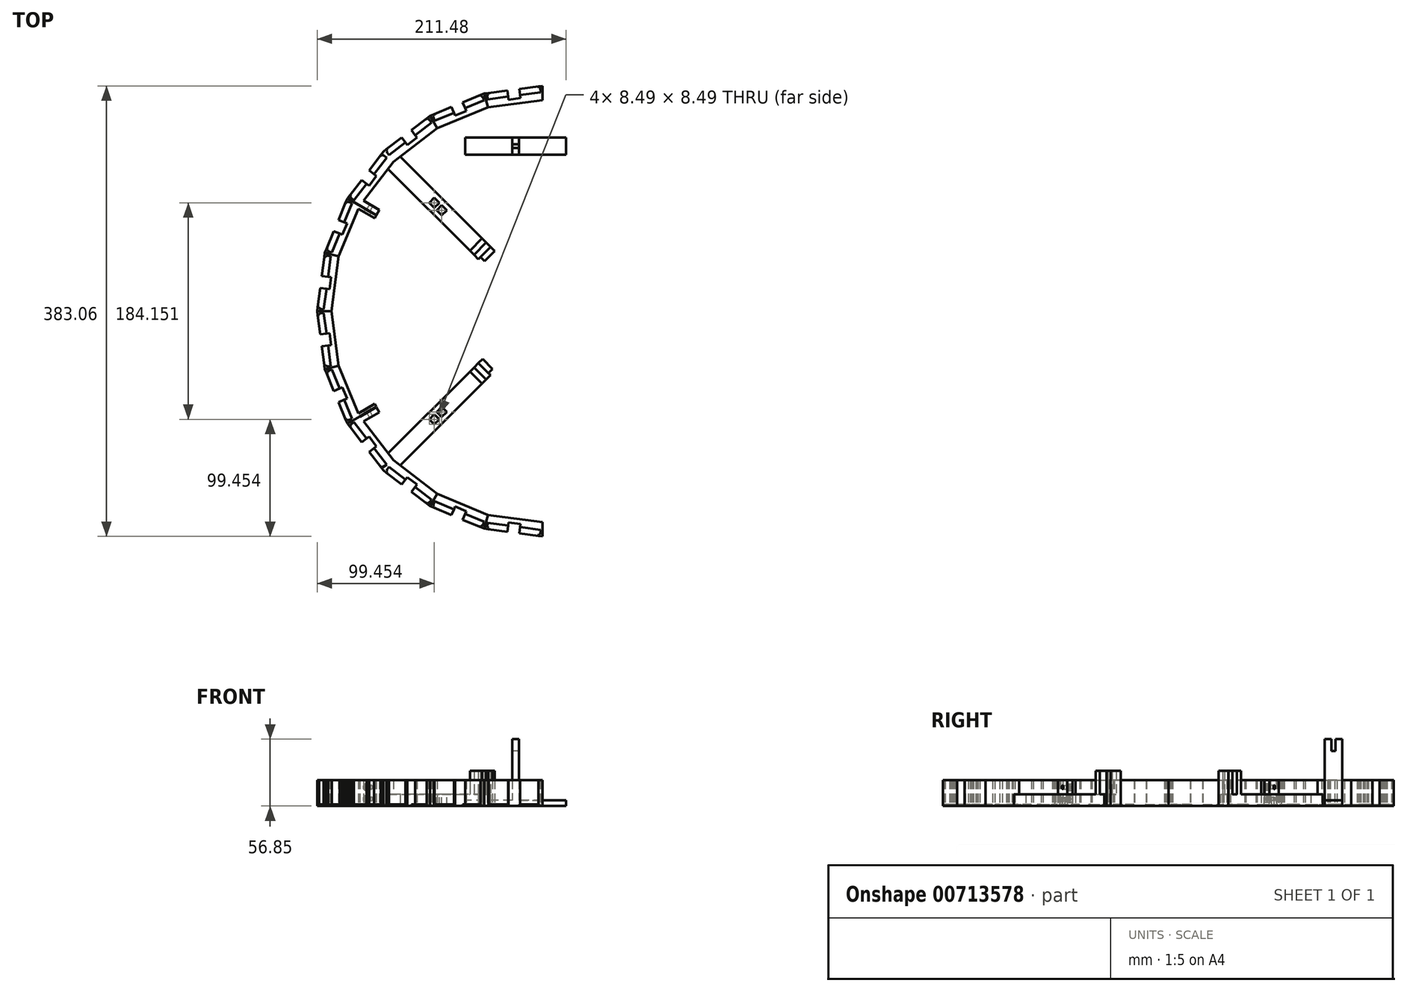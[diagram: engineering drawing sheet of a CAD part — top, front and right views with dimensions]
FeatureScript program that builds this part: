
annotation { "Feature Type Name" : "Feature", "Feature Type Description" : "" }
export const myFeature = defineFeature(function(context is Context, id is Id, definition is map)
    precondition{}
    {
        {
            var Q0;
            Q0=qCreatedBy(makeId("Top.planeOp"),FACE);
            var sketch = newSketch(context, id + "F0", { "sketchPlane" : qUnion([Q0])});
            skCircle(sketch, "E0.cCircle", {"center": v(0, 0) * mm, "radius": 75 * mm, "construction": true});
            skLineSegment(sketch, "E0.0", {"start": v(75, 31.07) * mm, "end": v(75, -31.07) * mm, "construction": true});
            skLineSegment(sketch, "E0.1", {"start": v(75, -31.07) * mm, "end": v(31.07, -75) * mm, "construction": true});
            skLineSegment(sketch, "E0.2", {"start": v(31.07, -75) * mm, "end": v(-31.07, -75) * mm, "construction": true});
            skLineSegment(sketch, "E0.3", {"start": v(-31.07, -75) * mm, "end": v(-75, -31.07) * mm, "construction": true});
            skLineSegment(sketch, "E0.4", {"start": v(-75, -31.07) * mm, "end": v(-75, 31.07) * mm, "construction": true});
            skLineSegment(sketch, "E0.5", {"start": v(-75, 31.07) * mm, "end": v(-31.07, 75) * mm, "construction": true});
            skLineSegment(sketch, "E0.6", {"start": v(-31.07, 75) * mm, "end": v(31.07, 75) * mm, "construction": true});
            skLineSegment(sketch, "E0.7", {"start": v(31.07, 75) * mm, "end": v(75, 31.07) * mm, "construction": true});
            skPoint(sketch, "E0.0.midPoint", {"position": v(74.36, -9.79) * mm});
            skPoint(sketch, "E1.endSnap0", {"position": v(0, -75) * mm});
            skArc(sketch, "E2.cCircle", {"start": v(0.47, 189.9) * mm, "mid": v(-189.9, 0.2) * mm, "end": v(0.07, -189.9) * mm, "construction": true});
            skLineSegment(sketch, "E2.1", {"start": v(0, -191.53) * mm, "end": v(-49.57, -185) * mm});
            skLineSegment(sketch, "E2.2", {"start": v(-49.57, -185) * mm, "end": v(-52.85, -183.65) * mm});
            skLineSegment(sketch, "E2.3", {"start": v(-95.77, -165.87) * mm, "end": v(-135.43, -135.43) * mm});
            skLineSegment(sketch, "E2.4", {"start": v(-135.43, -135.43) * mm, "end": v(-165.87, -95.77) * mm});
            skLineSegment(sketch, "E2.5", {"start": v(-165.87, -95.77) * mm, "end": v(-185, -49.57) * mm});
            skLineSegment(sketch, "E2.6", {"start": v(-185, -49.57) * mm, "end": v(-191.53, 0) * mm});
            skLineSegment(sketch, "E2.7", {"start": v(-191.53, 0) * mm, "end": v(-185, 49.57) * mm});
            skLineSegment(sketch, "E2.8", {"start": v(-185, 49.57) * mm, "end": v(-165.91, 95.67) * mm});
            skLineSegment(sketch, "E2.9", {"start": v(-165.81, 95.85) * mm, "end": v(-135.43, 135.43) * mm});
            skLineSegment(sketch, "E2.10", {"start": v(-135.43, 135.43) * mm, "end": v(-95.77, 165.87) * mm});
            skLineSegment(sketch, "E2.11", {"start": v(-95.77, 165.87) * mm, "end": v(-49.57, 185) * mm});
            skLineSegment(sketch, "E2.12", {"start": v(-49.57, 185) * mm, "end": v(0.47, 191.6) * mm});
            skLineSegment(sketch, "E3", {"start": v(0, 0) * mm, "end": v(-188.27, 24.79) * mm, "construction": true});
            skLineSegment(sketch, "E4.0", {"start": v(-46.44, 173.32) * mm, "end": v(0.46, 179.49) * mm});
            skLineSegment(sketch, "E4.1", {"start": v(-89.71, 155.39) * mm, "end": v(-46.44, 173.32) * mm});
            skLineSegment(sketch, "E4.2", {"start": v(-126.88, -126.88) * mm, "end": v(-155.39, -89.71) * mm});
            skLineSegment(sketch, "E4.3", {"start": v(-89.71, -155.39) * mm, "end": v(-126.88, -126.88) * mm});
            skLineSegment(sketch, "E4.4", {"start": v(-46.44, -173.32) * mm, "end": v(-89.71, -155.39) * mm});
            skLineSegment(sketch, "E4.5", {"start": v(0.5, -179.5) * mm, "end": v(-46.44, -173.32) * mm});
            skLineSegment(sketch, "E4.6", {"start": v(-155.39, -89.71) * mm, "end": v(-173.32, -46.44) * mm});
            skLineSegment(sketch, "E4.7", {"start": v(-173.32, -46.44) * mm, "end": v(-179.43, 0) * mm});
            skLineSegment(sketch, "E4.9", {"start": v(-173.32, 46.44) * mm, "end": v(-155.43, 89.62) * mm});
            skLineSegment(sketch, "E4.10", {"start": v(-155.33, 89.8) * mm, "end": v(-126.88, 126.88) * mm});
            skLineSegment(sketch, "E4.11", {"start": v(-126.88, 126.88) * mm, "end": v(-89.71, 155.39) * mm});
            skLineSegment(sketch, "E5", {"start": v(-72.67, -175.44) * mm, "end": v(-70.64, -170.54) * mm, "construction": true});
            skLineSegment(sketch, "E6", {"start": v(-65.88, -172.51) * mm, "end": v(-49.62, -179.25) * mm});
            skLineSegment(sketch, "E7", {"start": v(-75.4, -168.57) * mm, "end": v(-91.66, -161.84) * mm});
            skLineSegment(sketch, "E8", {"start": v(-49.62, -179.25) * mm, "end": v(-51.15, -182.94) * mm});
            skLineSegment(sketch, "E9", {"start": v(-91.66, -161.84) * mm, "end": v(-93.2, -165.53) * mm});
            skLineSegment(sketch, "E10", {"start": v(-93.2, -165.53) * mm, "end": v(-91.99, -166.03) * mm});
            skLineSegment(sketch, "E11", {"start": v(-91.99, -166.03) * mm, "end": v(-92.49, -167.23) * mm});
            skLineSegment(sketch, "E12", {"start": v(-51.15, -182.94) * mm, "end": v(-52.35, -182.45) * mm});
            skLineSegment(sketch, "E13", {"start": v(-52.35, -182.45) * mm, "end": v(-52.85, -183.65) * mm});
            skLineSegment(sketch, "E14.trimOffspring", {"start": v(-92.49, -167.23) * mm, "end": v(-95.77, -165.87) * mm});
            skLineSegment(sketch, "E15", {"start": v(-72.67, -175.44) * mm, "end": v(-69.65, -168.14) * mm, "construction": true});
            skLineSegment(sketch, "E16", {"start": v(-69.65, -168.14) * mm, "end": v(-64.89, -170.11) * mm});
            skLineSegment(sketch, "E17", {"start": v(-69.65, -168.14) * mm, "end": v(-74.4, -166.17) * mm});
            skLineSegment(sketch, "E18", {"start": v(-74.4, -166.17) * mm, "end": v(-75.4, -168.57) * mm});
            skLineSegment(sketch, "E19", {"start": v(-64.89, -170.11) * mm, "end": v(-65.88, -172.51) * mm});
            skLineSegment(sketch, "E20", {"start": v(-49.57, -185) * mm, "end": v(-46.44, -173.32) * mm});
            skLineSegment(sketch, "E21", {"start": v(-95.77, -165.87) * mm, "end": v(-89.71, -155.39) * mm});
            skLineSegment(sketch, "E22", {"start": v(-52.85, -183.65) * mm, "end": v(-92.49, -167.23) * mm});
            skLineSegment(sketch, "E23", {"start": v(-75.4, -168.57) * mm, "end": v(-77.43, -173.47) * mm});
            skLineSegment(sketch, "E24", {"start": v(-65.88, -172.51) * mm, "end": v(-67.91, -177.4) * mm, "construction": true});
            skLineSegment(sketch, "E25", {"start": v(-67.91, -177.4) * mm, "end": v(-65.88, -172.51) * mm});
            skLineSegment(sketch, "E26", {"start": v(-77.43, -173.47) * mm, "end": v(-75.4, -168.57) * mm, "construction": true});
            skLineSegment(sketch, "E27", {"start": v(-53.03, 53.03) * mm, "end": v(-126.88, 126.88) * mm, "construction": true});
            skLineSegment(sketch, "E28.0", {"start": v(-47.87, 58.2) * mm, "end": v(-121.03, 131.36) * mm});
            skLineSegment(sketch, "E29.0", {"start": v(-58.2, 47.87) * mm, "end": v(-131.36, 121.03) * mm});
            skLineSegment(sketch, "E30", {"start": v(-61.73, 51.4) * mm, "end": v(-51.4, 61.73) * mm});
            skLineSegment(sketch, "E31", {"start": v(-47.87, 58.2) * mm, "end": v(-44.2, 54.52) * mm});
            skLineSegment(sketch, "E32", {"start": v(-58.2, 47.87) * mm, "end": v(-54.52, 44.2) * mm});
            skLineSegment(sketch, "E33", {"start": v(-54.52, 44.2) * mm, "end": v(-44.2, 54.52) * mm});
            skLineSegment(sketch, "E34", {"start": v(-44.2, 54.52) * mm, "end": v(-40.66, 50.98) * mm});
            skLineSegment(sketch, "E35", {"start": v(-40.66, 50.98) * mm, "end": v(-49.14, 42.5) * mm});
            skLineSegment(sketch, "E36", {"start": v(-49.14, 42.5) * mm, "end": v(-52.68, 46.03) * mm});
            skLineSegment(sketch, "E37", {"start": v(-47.87, 58.2) * mm, "end": v(-58.2, 47.87) * mm});
            skLineSegment(sketch, "E38.1.0", {"start": v(-50.98, -40.66) * mm, "end": v(-42.5, -49.14) * mm});
            skLineSegment(sketch, "E38.1.1", {"start": v(-54.52, -44.2) * mm, "end": v(-50.98, -40.66) * mm});
            skLineSegment(sketch, "E38.1.2", {"start": v(-58.2, -47.87) * mm, "end": v(-54.52, -44.2) * mm});
            skLineSegment(sketch, "E38.1.3", {"start": v(-58.2, -47.87) * mm, "end": v(-47.87, -58.2) * mm});
            skLineSegment(sketch, "E38.1.4", {"start": v(-51.4, -61.73) * mm, "end": v(-61.73, -51.4) * mm});
            skLineSegment(sketch, "E38.1.5", {"start": v(-44.2, -54.52) * mm, "end": v(-54.52, -44.2) * mm});
            skLineSegment(sketch, "E38.1.6", {"start": v(-47.87, -58.2) * mm, "end": v(-44.2, -54.52) * mm});
            skLineSegment(sketch, "E38.1.7", {"start": v(-47.87, -58.2) * mm, "end": v(-121.03, -131.36) * mm});
            skLineSegment(sketch, "E38.1.8", {"start": v(-58.2, -47.87) * mm, "end": v(-131.36, -121.03) * mm});
            skLineSegment(sketch, "E38.anchor1", {"start": v(0, 0) * mm, "end": v(-49.14, 42.5) * mm, "construction": true});
            skLineSegment(sketch, "E38.anchor2", {"start": v(0, 0) * mm, "end": v(-42.5, -49.14) * mm, "construction": true});
            skLineSegment(sketch, "E39", {"start": v(-179.43, 0) * mm, "end": v(-191.53, 0) * mm});
            skLineSegment(sketch, "E40", {"start": v(0.07, -189.9) * mm, "end": v(0.47, 191.6) * mm, "construction": true});
            skPoint(sketch, "E41.orphan", {"position": v(0.5, 222.53) * mm});
            skLineSegment(sketch, "E42", {"start": v(-42.5, -49.14) * mm, "end": v(-46.03, -52.68) * mm});
            skLineSegment(sketch, "E43", {"start": v(-179.43, 0) * mm, "end": v(-173.32, 46.44) * mm});
            skLineSegment(sketch, "E44", {"start": v(-141.21, 81.64) * mm, "end": v(-138.71, 85.98) * mm});
            skLineSegment(sketch, "E45", {"start": v(-138.71, 85.98) * mm, "end": v(-152.26, 93.8) * mm});
            skLineSegment(sketch, "E46", {"start": v(-141.31, 81.47) * mm, "end": v(-142.76, 78.96) * mm});
            skLineSegment(sketch, "E47", {"start": v(-142.76, 78.96) * mm, "end": v(-156.55, 86.92) * mm});
            skLineSegment(sketch, "E48", {"start": v(0, 0) * mm, "end": v(-165.87, 95.77) * mm, "construction": true});
            skLineSegment(sketch, "E49", {"start": v(-141.21, 81.64) * mm, "end": v(-165.81, 95.85) * mm});
            skLineSegment(sketch, "E50", {"start": v(-165.91, 95.67) * mm, "end": v(-141.31, 81.47) * mm});
            skLineSegment(sketch, "E51", {"start": v(-155.43, 89.62) * mm, "end": v(-155.33, 89.8) * mm});
            skLineSegment(sketch, "E52", {"start": v(-165.91, 95.67) * mm, "end": v(-165.87, 95.77) * mm});
            skLineSegment(sketch, "E53", {"start": v(-165.87, 95.77) * mm, "end": v(-165.81, 95.85) * mm});
            skLineSegment(sketch, "E54.1.0", {"start": v(-141.31, -81.47) * mm, "end": v(-142.76, -78.96) * mm});
            skLineSegment(sketch, "E54.1.2", {"start": v(-141.31, -81.47) * mm, "end": v(-165.91, -95.67) * mm});
            skLineSegment(sketch, "E54.1.3", {"start": v(-165.81, -95.85) * mm, "end": v(-141.21, -81.64) * mm});
            skLineSegment(sketch, "E54.1.4", {"start": v(-155.33, -89.8) * mm, "end": v(-155.43, -89.62) * mm});
            skLineSegment(sketch, "E54.1.5", {"start": v(-138.71, -85.98) * mm, "end": v(-152.26, -93.8) * mm});
            skLineSegment(sketch, "E54.1.6", {"start": v(-141.21, -81.64) * mm, "end": v(-138.71, -85.98) * mm});
            skLineSegment(sketch, "E54.1.7", {"start": v(-165.81, -95.85) * mm, "end": v(-165.87, -95.77) * mm});
            skLineSegment(sketch, "E54.1.8", {"start": v(-165.87, -95.77) * mm, "end": v(-165.91, -95.67) * mm});
            skLineSegment(sketch, "E54.1.9", {"start": v(0, 0) * mm, "end": v(-165.87, -95.77) * mm, "construction": true});
            skLineSegment(sketch, "E54.anchor1", {"start": v(0, 0) * mm, "end": v(-165.91, 95.67) * mm, "construction": true});
            skLineSegment(sketch, "E54.anchor2", {"start": v(0, 0) * mm, "end": v(-165.81, -95.85) * mm, "construction": true});
            skLineSegment(sketch, "E55", {"start": v(-142.76, -78.96) * mm, "end": v(-156.55, -86.92) * mm});
            skSolve(sketch);
        }
        {
            var Q0;
            Q0=makeQuery(id+"F0.imprint","IMPRINT",FACE,{"disambiguationData":[TD([[makeQuery(id+"F0.imprint","IMPRINT",EDGE,{"derivedFrom":sQuery(id+"F0.wireOp",EDGE,"E2.2")}),-1.0]])]});
            extrude(context, id + "F1", {"entities" : qUnion([Q0]), "depth" : 22 * mm, "offsetDistance" : 25 * mm});
        }
        {
            var Q0;
            Q0=makeQuery(id+"F0.imprint","IMPRINT",FACE,{"disambiguationData":[TD([[makeQuery(id+"F0.imprint","IMPRINT",EDGE,{"derivedFrom":sQuery(id+"F0.wireOp",EDGE,"E6")}),-1.0]])]});
            var Q1;
            Q1=makeQuery(id+"F0.imprint","IMPRINT",FACE,{"disambiguationData":[TD([[makeQuery(id+"F0.imprint","IMPRINT",EDGE,{"derivedFrom":sQuery(id+"F0.wireOp",EDGE,"E7")}),1.0]])]});
            extrude(context, id + "F2", {"entities" : qUnion([Q0, Q1]), "operationType" : NewBodyOperationType.ADD, "depth" : 1.5 * mm, "offsetDistance" : 25 * mm});
        }
        {
            var Q0;
            Q0=qCreatedBy(makeId("Front.planeOp"),FACE);
            var sketch = newSketch(context, id + "F3", { "sketchPlane" : qUnion([Q0])});
            skLineSegment(sketch, "E56", {"start": v(0, 0) * mm, "end": v(0, 23.59) * mm, "construction": true});
            skSolve(sketch);
        }
        {
            var Q0;
            Q0=makeQuery(id+"F1.opExtrude","SWEPT_BODY",BODY,{"disambiguationData":[OSD([sQuery(id+"F0.wireOp",EDGE,"E2.2"),sQuery(id+"F0.wireOp",EDGE,"E4.4"),sQuery(id+"F0.wireOp",EDGE,"E6"),sQuery(id+"F0.wireOp",EDGE,"E7"),sQuery(id+"F0.wireOp",EDGE,"E8"),sQuery(id+"F0.wireOp",EDGE,"E9"),sQuery(id+"F0.wireOp",EDGE,"E10"),sQuery(id+"F0.wireOp",EDGE,"E11"),sQuery(id+"F0.wireOp",EDGE,"E12"),sQuery(id+"F0.wireOp",EDGE,"E13"),sQuery(id+"F0.wireOp",EDGE,"E14.trimOffspring"),sQuery(id+"F0.wireOp",EDGE,"E16"),sQuery(id+"F0.wireOp",EDGE,"E17"),sQuery(id+"F0.wireOp",EDGE,"E18"),sQuery(id+"F0.wireOp",EDGE,"E19"),sQuery(id+"F0.wireOp",EDGE,"E20"),sQuery(id+"F0.wireOp",EDGE,"E21")])]});
            var Q1;
            Q1=sQuery(id+"F3.wireOp",EDGE,"E56");
            transform(context, id + "F4", {"entities" : qUnion([Q0]), "transformType" : TransformType.ROTATION, "transformAxis" : qUnion([Q1]), "angle" : 15 * degree, "makeCopy" : true});
        }
        {
            var Q0;
            Q0=makeQuery(id+"F1.opExtrude","SWEPT_BODY",BODY,{"disambiguationData":[OSD([sQuery(id+"F0.wireOp",EDGE,"E2.2"),sQuery(id+"F0.wireOp",EDGE,"E4.4"),sQuery(id+"F0.wireOp",EDGE,"E6"),sQuery(id+"F0.wireOp",EDGE,"E7"),sQuery(id+"F0.wireOp",EDGE,"E8"),sQuery(id+"F0.wireOp",EDGE,"E9"),sQuery(id+"F0.wireOp",EDGE,"E10"),sQuery(id+"F0.wireOp",EDGE,"E11"),sQuery(id+"F0.wireOp",EDGE,"E12"),sQuery(id+"F0.wireOp",EDGE,"E13"),sQuery(id+"F0.wireOp",EDGE,"E14.trimOffspring"),sQuery(id+"F0.wireOp",EDGE,"E16"),sQuery(id+"F0.wireOp",EDGE,"E17"),sQuery(id+"F0.wireOp",EDGE,"E18"),sQuery(id+"F0.wireOp",EDGE,"E19"),sQuery(id+"F0.wireOp",EDGE,"E20"),sQuery(id+"F0.wireOp",EDGE,"E21")])]});
            var Q1;
            Q1=sQuery(id+"F3.wireOp",EDGE,"E56");
            circularPattern(context, id + "F5", {"entities" : qUnion([Q0]), "axis" : qUnion([Q1]), "angle" : 150 * degree, "instanceCount" : 11, "oppositeDirection" : true, "equalSpace" : true});
        }
        {
            var Q0;
            {var subQ3=sQuery(id+"F0.wireOp",EDGE,"E30");Q0=makeQuery(id+"F0.imprint","IMPRINT",FACE,{"disambiguationData":[TD([[makeQuery(id+"F0.imprint","IMPRINT",EDGE,{"derivedFrom":subQ3}),1.0]])]});}
            var Q1;
            {var subQ2=sQuery(id+"F0.wireOp",EDGE,"E30");Q1=makeQuery(id+"F0.imprint","IMPRINT",FACE,{"disambiguationData":[TD([[makeQuery(id+"F0.imprint","IMPRINT",EDGE,{"derivedFrom":subQ2}),-1.0]])]});}
            var Q2;
            {var subQ1=sQuery(id+"F0.wireOp",EDGE,"E31");Q2=makeQuery(id+"F0.imprint","IMPRINT",FACE,{"disambiguationData":[TD([[makeQuery(id+"F0.imprint","IMPRINT",EDGE,{"derivedFrom":subQ1}),-1.0]])]});}
            var Q3;
            {var subQ0=sQuery(id+"F0.wireOp",EDGE,"E34");Q3=makeQuery(id+"F0.imprint","IMPRINT",FACE,{"disambiguationData":[TD([[makeQuery(id+"F0.imprint","IMPRINT",EDGE,{"derivedFrom":subQ0}),-1.0]])]});}
            var Q4;
            {var subQ1=sQuery(id+"F0.wireOp",EDGE,"E38.1.4");Q4=makeQuery(id+"F0.imprint","IMPRINT",FACE,{"disambiguationData":[TD([[makeQuery(id+"F0.imprint","IMPRINT",EDGE,{"derivedFrom":subQ1}),1.0]])]});}
            var Q5;
            {var subQ0=sQuery(id+"F0.wireOp",EDGE,"E38.1.3");Q5=makeQuery(id+"F0.imprint","IMPRINT",FACE,{"disambiguationData":[TD([[makeQuery(id+"F0.imprint","IMPRINT",EDGE,{"derivedFrom":subQ0}),-1.0]])]});}
            var Q6;
            {var subQ1=sQuery(id+"F0.wireOp",EDGE,"E38.1.2");Q6=makeQuery(id+"F0.imprint","IMPRINT",FACE,{"disambiguationData":[TD([[makeQuery(id+"F0.imprint","IMPRINT",EDGE,{"derivedFrom":subQ1}),-1.0]])]});}
            var Q7;
            Q7=makeQuery(id+"F0.imprint","IMPRINT",FACE,{"disambiguationData":[TD([[makeQuery(id+"F0.imprint","IMPRINT",EDGE,{"derivedFrom":sQuery(id+"F0.wireOp",EDGE,"E38.1.0")}),-1.0]])]});
            extrude(context, id + "F6", {"entities" : qUnion([Q0, Q1, Q2, Q3, Q4, Q5, Q6, Q7]), "operationType" : NewBodyOperationType.ADD, "depth" : 5 * mm, "offsetDistance" : 25 * mm});
        }
        {
            var Q0;
            {var subQ2=sQuery(id+"F0.wireOp",EDGE,"E30");Q0=makeQuery(id+"F0.imprint","IMPRINT",FACE,{"disambiguationData":[TD([[makeQuery(id+"F0.imprint","IMPRINT",EDGE,{"derivedFrom":subQ2}),-1.0]])]});}
            var Q1;
            {var subQ0=sQuery(id+"F0.wireOp",EDGE,"E34");Q1=makeQuery(id+"F0.imprint","IMPRINT",FACE,{"disambiguationData":[TD([[makeQuery(id+"F0.imprint","IMPRINT",EDGE,{"derivedFrom":subQ0}),-1.0]])]});}
            var Q2;
            Q2=makeQuery(id+"F0.imprint","IMPRINT",FACE,{"disambiguationData":[TD([[makeQuery(id+"F0.imprint","IMPRINT",EDGE,{"derivedFrom":sQuery(id+"F0.wireOp",EDGE,"E38.1.0")}),-1.0]])]});
            var Q3;
            {var subQ0=sQuery(id+"F0.wireOp",EDGE,"E38.1.3");Q3=makeQuery(id+"F0.imprint","IMPRINT",FACE,{"disambiguationData":[TD([[makeQuery(id+"F0.imprint","IMPRINT",EDGE,{"derivedFrom":subQ0}),-1.0]])]});}
            extrude(context, id + "F7", {"entities" : qUnion([Q0, Q1, Q2, Q3]), "operationType" : NewBodyOperationType.ADD, "depth" : 30 * mm, "offsetDistance" : 25 * mm});
        }
        {
            var Q0;
            Q0=makeQuery(id+"F0.imprint","IMPRINT",FACE,{"disambiguationData":[TD([[makeQuery(id+"F0.imprint","IMPRINT",EDGE,{"derivedFrom":sQuery(id+"F0.wireOp",EDGE,"GCTjbCZ3-rWJ8-3Bt5-pqQ0-WsXmROxkx1kK")}),1.0]])]});
            var Q1;
            {var subQ0=sQuery(id+"F0.wireOp",EDGE,"EZpf3oR2-MSXJ-6veG-nYI6-mttKvzj23KY3");Q1=makeQuery(id+"F0.imprint","IMPRINT",FACE,{"disambiguationData":[TD([[makeQuery(id+"F0.imprint","IMPRINT",EDGE,{"derivedFrom":subQ0}),-1.0]])]});}
            var Q2;
            {var subQ3=sQuery(id+"F0.wireOp",EDGE,"E30");Q2=makeQuery(id+"F0.imprint","IMPRINT",FACE,{"disambiguationData":[TD([[makeQuery(id+"F0.imprint","IMPRINT",EDGE,{"derivedFrom":subQ3}),1.0]])]});}
            var Q3;
            {var subQ0=sQuery(id+"F0.wireOp",EDGE,"E34");Q3=makeQuery(id+"F0.imprint","IMPRINT",FACE,{"disambiguationData":[TD([[makeQuery(id+"F0.imprint","IMPRINT",EDGE,{"derivedFrom":subQ0}),-1.0]])]});}
            var Q4;
            Q4=makeQuery(id+"F0.imprint","IMPRINT",FACE,{"disambiguationData":[TD([[makeQuery(id+"F0.imprint","IMPRINT",EDGE,{"derivedFrom":sQuery(id+"F0.wireOp",EDGE,"E38.1.0")}),-1.0]])]});
            var Q5;
            {var subQ1=sQuery(id+"F0.wireOp",EDGE,"E38.1.4");Q5=makeQuery(id+"F0.imprint","IMPRINT",FACE,{"disambiguationData":[TD([[makeQuery(id+"F0.imprint","IMPRINT",EDGE,{"derivedFrom":subQ1}),1.0]])]});}
            var Q6;
            {var subQ2=sQuery(id+"F0.wireOp",EDGE,"E30");Q6=makeQuery(id+"F0.imprint","IMPRINT",FACE,{"disambiguationData":[TD([[makeQuery(id+"F0.imprint","IMPRINT",EDGE,{"derivedFrom":subQ2}),-1.0]])]});}
            var Q7;
            {var subQ1=sQuery(id+"F0.wireOp",EDGE,"E31");Q7=makeQuery(id+"F0.imprint","IMPRINT",FACE,{"disambiguationData":[TD([[makeQuery(id+"F0.imprint","IMPRINT",EDGE,{"derivedFrom":subQ1}),-1.0]])]});}
            var Q8;
            {var subQ1=sQuery(id+"F0.wireOp",EDGE,"E38.1.2");Q8=makeQuery(id+"F0.imprint","IMPRINT",FACE,{"disambiguationData":[TD([[makeQuery(id+"F0.imprint","IMPRINT",EDGE,{"derivedFrom":subQ1}),-1.0]])]});}
            var Q9;
            {var subQ0=sQuery(id+"F0.wireOp",EDGE,"E38.1.3");Q9=makeQuery(id+"F0.imprint","IMPRINT",FACE,{"disambiguationData":[TD([[makeQuery(id+"F0.imprint","IMPRINT",EDGE,{"derivedFrom":subQ0}),-1.0]])]});}
            extrude(context, id + "F8", {"entities" : qUnion([Q0, Q1, Q2, Q3, Q4, Q5, Q6, Q7, Q8, Q9]), "operationType" : NewBodyOperationType.ADD, "depth" : 10 * mm, "offsetDistance" : 25 * mm});
        }
        {
            var Q0;
            {var subQ0=sQuery(id+"F0.wireOp",EDGE,"E34");var subQ1=sQuery(id+"F0.wireOp",EDGE,"E31");var subQ2=sQuery(id+"F0.wireOp",EDGE,"E28.0");var subQ3=sQuery(id+"F0.wireOp",EDGE,"E32");var subQ4=sQuery(id+"F0.wireOp",EDGE,"E29.0");var subQ5=makeQuery(id+"F1.opExtrude","SWEPT_FACE",FACE,{"disambiguationData":[OSD([sQuery(id+"F0.wireOp",EDGE,"E4.4")])]});Q0=makeQuery(id+"F8.boolean.opBoolean","SPLIT",FACE,{"disambiguationData":[TD([makeQuery(id+"F5.opPattern","COPY",FACE,{"derivedFrom":subQ5,"instanceName":"7"})])],"derivedFrom":makeQuery(id+"F8.opExtrude","CAP_FACE",FACE,{"disambiguationData":[OSD([sQuery(id+"F0.wireOp",EDGE,"E4.10"),sQuery(id+"F0.wireOp",EDGE,"E4.11"),subQ2,subQ4,subQ1,subQ3,sQuery(id+"F0.wireOp",EDGE,"E33"),subQ0,sQuery(id+"F0.wireOp",EDGE,"E35"),sQuery(id+"F0.wireOp",EDGE,"E36")])],"isStart":false})});}
            var sketch = newSketch(context, id + "F9", { "sketchPlane" : qUnion([Q0])});
            skLineSegment(sketch, "E57.0", {"start": v(-53.03, 53.03) * mm, "end": v(-126.88, 126.88) * mm, "construction": true});
            skLineSegment(sketch, "E58", {"start": v(-89.95, 89.95) * mm, "end": v(-87.83, 92.08) * mm});
            skLineSegment(sketch, "E59", {"start": v(-89.95, 89.95) * mm, "end": v(-92.08, 87.83) * mm});
            skLineSegment(sketch, "E60", {"start": v(-87.83, 92.08) * mm, "end": v(-92.08, 96.32) * mm});
            skLineSegment(sketch, "E61", {"start": v(-92.08, 96.32) * mm, "end": v(-96.32, 92.08) * mm});
            skLineSegment(sketch, "E62", {"start": v(-96.32, 92.08) * mm, "end": v(-92.08, 87.83) * mm});
            skLineSegment(sketch, "E63", {"start": v(-87.83, 92.08) * mm, "end": v(-85.71, 89.95) * mm, "construction": true});
            skLineSegment(sketch, "E64", {"start": v(-85.71, 89.95) * mm, "end": v(-89.95, 85.71) * mm});
            skLineSegment(sketch, "E65", {"start": v(-89.95, 85.71) * mm, "end": v(-85.71, 81.47) * mm});
            skLineSegment(sketch, "E66", {"start": v(-85.71, 81.47) * mm, "end": v(-81.47, 85.71) * mm});
            skLineSegment(sketch, "E67", {"start": v(-81.47, 85.71) * mm, "end": v(-85.71, 89.95) * mm});
            skLineSegment(sketch, "E68.1.0", {"start": v(-89.95, -85.71) * mm, "end": v(-85.71, -89.95) * mm});
            skLineSegment(sketch, "E68.1.1", {"start": v(-85.71, -81.47) * mm, "end": v(-89.95, -85.71) * mm});
            skLineSegment(sketch, "E68.1.2", {"start": v(-81.47, -85.71) * mm, "end": v(-85.71, -81.47) * mm});
            skLineSegment(sketch, "E68.1.3", {"start": v(-85.71, -89.95) * mm, "end": v(-81.47, -85.71) * mm});
            skLineSegment(sketch, "E68.1.4", {"start": v(-53.03, -53.03) * mm, "end": v(-126.88, -126.88) * mm, "construction": true});
            skLineSegment(sketch, "E68.1.5", {"start": v(-89.95, -89.95) * mm, "end": v(-92.08, -87.83) * mm});
            skLineSegment(sketch, "E68.1.6", {"start": v(-92.08, -87.83) * mm, "end": v(-96.32, -92.08) * mm});
            skLineSegment(sketch, "E68.1.7", {"start": v(-96.32, -92.08) * mm, "end": v(-92.08, -96.32) * mm});
            skLineSegment(sketch, "E68.1.8", {"start": v(-92.08, -96.32) * mm, "end": v(-87.83, -92.08) * mm});
            skLineSegment(sketch, "E68.1.9", {"start": v(-89.95, -89.95) * mm, "end": v(-87.83, -92.08) * mm});
            skLineSegment(sketch, "E68.1.10", {"start": v(-92.08, -87.83) * mm, "end": v(-89.95, -85.71) * mm, "construction": true});
            skPoint(sketch, "E68.center", {"position": v(0, 0) * mm});
            skSolve(sketch);
        }
        {
            var Q0;
            Q0=makeQuery(id+"F9.imprint","IMPRINT",FACE,{"disambiguationData":[TD([[makeQuery(id+"F9.imprint","IMPRINT",EDGE,{"derivedFrom":sQuery(id+"F9.wireOp",EDGE,"E68.1.0")}),1.0]])]});
            var Q1;
            Q1=makeQuery(id+"F9.imprint","IMPRINT",FACE,{"disambiguationData":[TD([[makeQuery(id+"F9.imprint","IMPRINT",EDGE,{"derivedFrom":sQuery(id+"F9.wireOp",EDGE,"E68.1.5")}),1.0]])]});
            extrude(context, id + "F10", {"entities" : qUnion([Q0, Q1]), "operationType" : NewBodyOperationType.REMOVE, "oppositeDirection" : true, "depth" : 25 * mm, "offsetDistance" : 25 * mm});
        }
        {
            var Q0;
            Q0=makeQuery(id+"F9.imprint","IMPRINT",FACE,{"disambiguationData":[TD([[makeQuery(id+"F9.imprint","IMPRINT",EDGE,{"derivedFrom":sQuery(id+"F9.wireOp",EDGE,"E64")}),1.0]])]});
            var Q1;
            Q1=makeQuery(id+"F9.imprint","IMPRINT",FACE,{"disambiguationData":[TD([[makeQuery(id+"F9.imprint","IMPRINT",EDGE,{"derivedFrom":sQuery(id+"F9.wireOp",EDGE,"E58")}),1.0]])]});
            extrude(context, id + "F11", {"entities" : qUnion([Q0, Q1]), "operationType" : NewBodyOperationType.REMOVE, "oppositeDirection" : true, "depth" : 25 * mm, "offsetDistance" : 25 * mm});
        }
        {
            var Q0;
            Q0=qCreatedBy(makeId("Top.planeOp"),FACE);
            var sketch = newSketch(context, id + "F12", { "sketchPlane" : qUnion([Q0])});
            skLineSegment(sketch, "E69", {"start": v(-25.85, 147.69) * mm, "end": v(-20.05, 147.69) * mm});
            skLineSegment(sketch, "E70", {"start": v(-20.05, 147.69) * mm, "end": v(-20.05, 141.89) * mm});
            skLineSegment(sketch, "E71", {"start": v(-20.05, 141.89) * mm, "end": v(-25.85, 141.89) * mm});
            skLineSegment(sketch, "E72", {"start": v(-25.85, 141.89) * mm, "end": v(-25.85, 147.69) * mm});
            skLineSegment(sketch, "E73", {"start": v(-25.85, 141.89) * mm, "end": v(-25.85, 138.69) * mm, "construction": true});
            skLineSegment(sketch, "E74", {"start": v(-25.85, 138.69) * mm, "end": v(-20.05, 138.69) * mm});
            skLineSegment(sketch, "E75", {"start": v(-20.05, 138.69) * mm, "end": v(-20.05, 132.89) * mm});
            skLineSegment(sketch, "E76", {"start": v(-20.05, 132.89) * mm, "end": v(-25.85, 132.89) * mm});
            skLineSegment(sketch, "E77", {"start": v(-25.85, 132.89) * mm, "end": v(-25.85, 138.69) * mm});
            skLineSegment(sketch, "E78", {"start": v(-25.85, 147.69) * mm, "end": v(-65.85, 147.69) * mm});
            skLineSegment(sketch, "E79", {"start": v(-25.85, 132.89) * mm, "end": v(-65.85, 132.89) * mm});
            skLineSegment(sketch, "E80", {"start": v(-65.85, 132.89) * mm, "end": v(-65.85, 147.69) * mm});
            skLineSegment(sketch, "E81", {"start": v(-20.05, 147.69) * mm, "end": v(19.95, 147.69) * mm});
            skLineSegment(sketch, "E82", {"start": v(19.95, 147.69) * mm, "end": v(19.95, 132.89) * mm});
            skLineSegment(sketch, "E83", {"start": v(19.95, 132.89) * mm, "end": v(-20.05, 132.89) * mm});
            skLineSegment(sketch, "E84", {"start": v(-20.05, 138.69) * mm, "end": v(-20.05, 141.89) * mm});
            skLineSegment(sketch, "E85", {"start": v(-25.85, 138.69) * mm, "end": v(-25.85, 141.89) * mm});
            skSolve(sketch);
        }
        {
            var Q0;
            Q0=makeQuery(id+"F12.imprint","IMPRINT",FACE,{"disambiguationData":[TD([[makeQuery(id+"F12.imprint","IMPRINT",EDGE,{"derivedFrom":sQuery(id+"F12.wireOp",EDGE,"E71")}),1.0]])]});
            extrude(context, id + "F13", {"entities" : qUnion([Q0]), "depth" : 46.85 * mm, "offsetDistance" : 25 * mm});
        }
        {
            var Q0;
            Q0=makeQuery(id+"F12.imprint","IMPRINT",FACE,{"disambiguationData":[TD([[makeQuery(id+"F12.imprint","IMPRINT",EDGE,{"derivedFrom":sQuery(id+"F12.wireOp",EDGE,"E74")}),-1.0]])]});
            var Q1;
            Q1=makeQuery(id+"F12.imprint","IMPRINT",FACE,{"disambiguationData":[TD([[makeQuery(id+"F12.imprint","IMPRINT",EDGE,{"derivedFrom":sQuery(id+"F12.wireOp",EDGE,"E69")}),-1.0]])]});
            extrude(context, id + "F14", {"entities" : qUnion([Q0, Q1]), "operationType" : NewBodyOperationType.ADD, "depth" : 56.85 * mm, "offsetDistance" : 25 * mm});
        }
        {
            var Q0;
            Q0=makeQuery(id+"F12.imprint","IMPRINT",FACE,{"disambiguationData":[TD([[makeQuery(id+"F12.imprint","IMPRINT",EDGE,{"derivedFrom":sQuery(id+"F12.wireOp",EDGE,"E72")}),1.0]])]});
            var Q1;
            Q1=makeQuery(id+"F12.imprint","IMPRINT",FACE,{"disambiguationData":[TD([[makeQuery(id+"F12.imprint","IMPRINT",EDGE,{"derivedFrom":sQuery(id+"F12.wireOp",EDGE,"E70")}),1.0]])]});
            extrude(context, id + "F15", {"entities" : qUnion([Q0, Q1]), "operationType" : NewBodyOperationType.ADD, "depth" : 5 * mm, "offsetDistance" : 25 * mm});
        }
        {
            var Q0;
            {var subQ1=sQuery(id+"F0.wireOp",EDGE,"E51");Q0=makeQuery(id+"F0.imprint","IMPRINT",FACE,{"disambiguationData":[TD([[makeQuery(id+"F0.imprint","IMPRINT",EDGE,{"derivedFrom":subQ1}),1.0]])]});}
            var Q1;
            {var subQ0=sQuery(id+"F0.wireOp",EDGE,"E54.1.7");Q1=makeQuery(id+"F0.imprint","IMPRINT",FACE,{"disambiguationData":[TD([[makeQuery(id+"F0.imprint","IMPRINT",EDGE,{"derivedFrom":subQ0}),-1.0]])]});}
            extrude(context, id + "F16", {"entities" : qUnion([Q0, Q1]), "operationType" : NewBodyOperationType.REMOVE, "depth" : 26.5 * mm, "offsetDistance" : 25 * mm});
        }
        {
            var Q0;
            {var subQ4=sQuery(id+"F0.wireOp",EDGE,"E46");Q0=makeQuery(id+"F0.imprint","IMPRINT",FACE,{"disambiguationData":[TD([[makeQuery(id+"F0.imprint","IMPRINT",EDGE,{"derivedFrom":subQ4}),-1.0]])]});}
            extrude(context, id + "F17", {"entities" : qUnion([Q0]), "operationType" : NewBodyOperationType.ADD, "depth" : 22 * mm, "offsetDistance" : 25 * mm});
        }
        {
            var Q0;
            {var subQ4=sQuery(id+"F0.wireOp",EDGE,"E44");Q0=makeQuery(id+"F0.imprint","IMPRINT",FACE,{"disambiguationData":[TD([[makeQuery(id+"F0.imprint","IMPRINT",EDGE,{"derivedFrom":subQ4}),1.0]])]});}
            extrude(context, id + "F18", {"entities" : qUnion([Q0]), "operationType" : NewBodyOperationType.ADD, "depth" : 22 * mm, "offsetDistance" : 25 * mm});
        }
        {
            var Q0;
            {var subQ4=sQuery(id+"F0.wireOp",EDGE,"E54.1.0");Q0=makeQuery(id+"F0.imprint","IMPRINT",FACE,{"disambiguationData":[TD([[makeQuery(id+"F0.imprint","IMPRINT",EDGE,{"derivedFrom":subQ4}),1.0]])]});}
            extrude(context, id + "F19", {"entities" : qUnion([Q0]), "operationType" : NewBodyOperationType.ADD, "depth" : 22 * mm, "offsetDistance" : 25 * mm});
        }
        {
            var Q0;
            {var subQ3=sQuery(id+"F0.wireOp",EDGE,"E54.1.5");Q0=makeQuery(id+"F0.imprint","IMPRINT",FACE,{"disambiguationData":[TD([[makeQuery(id+"F0.imprint","IMPRINT",EDGE,{"derivedFrom":subQ3}),-1.0]])]});}
            extrude(context, id + "F20", {"entities" : qUnion([Q0]), "operationType" : NewBodyOperationType.ADD, "depth" : 22 * mm, "offsetDistance" : 25 * mm});
        }
        {
            var Q0;
            Q0=makeQuery(id+"F17.opExtrude","SWEPT_FACE",FACE,{"disambiguationData":[OSD([sQuery(id+"F0.wireOp",EDGE,"E47")])]});
            var sketch = newSketch(context, id + "F21", { "sketchPlane" : qUnion([Q0])});
            skPoint(sketch, "E86.0", {"position": v(-163.12, 22) * mm});
            skPoint(sketch, "E86.1", {"position": v(-163.12, 0) * mm});
            skLineSegment(sketch, "E87", {"start": v(-163.12, 22) * mm, "end": v(-163.12, 16) * mm, "construction": true});
            skLineSegment(sketch, "E88", {"start": v(-163.12, 16) * mm, "end": v(-171.12, 16) * mm, "construction": true});
            skLineSegment(sketch, "E89", {"start": v(-163.12, 0) * mm, "end": v(-163.12, 6) * mm, "construction": true});
            skLineSegment(sketch, "E90", {"start": v(-163.12, 6) * mm, "end": v(-171.12, 6) * mm, "construction": true});
            skCircle(sketch, "E91", {"center": v(-171.12, 16) * mm, "radius": 1 * mm});
            skCircle(sketch, "E92", {"center": v(-171.12, 16) * mm, "radius": 1.5 * mm});
            skCircle(sketch, "E93", {"center": v(-171.12, 16) * mm, "radius": 3 * mm});
            skCircle(sketch, "E94", {"center": v(-171.12, 6) * mm, "radius": 1 * mm});
            skCircle(sketch, "E95", {"center": v(-171.12, 6) * mm, "radius": 1.5 * mm});
            skCircle(sketch, "E96", {"center": v(-171.12, 6) * mm, "radius": 3 * mm});
            skSolve(sketch);
        }
        {
            var Q0;
            Q0=makeQuery(id+"F21.imprint","IMPRINT",FACE,{"disambiguationData":[TD([[makeQuery(id+"F21.imprint","IMPRINT",EDGE,{"derivedFrom":sQuery(id+"F21.wireOp",EDGE,"E91")}),1.0]])]});
            var Q1;
            Q1=makeQuery(id+"F21.imprint","IMPRINT",FACE,{"disambiguationData":[TD([[makeQuery(id+"F21.imprint","IMPRINT",EDGE,{"derivedFrom":sQuery(id+"F21.wireOp",EDGE,"E94")}),1.0]])]});
            extrude(context, id + "F22", {"entities" : qUnion([Q0, Q1]), "operationType" : NewBodyOperationType.REMOVE, "oppositeDirection" : true, "depth" : 10.4 * mm, "offsetDistance" : 25 * mm});
        }
        {
            var Q0;
            Q0=makeQuery(id+"F21.imprint","IMPRINT",FACE,{"disambiguationData":[TD([[makeQuery(id+"F21.imprint","IMPRINT",EDGE,{"derivedFrom":sQuery(id+"F21.wireOp",EDGE,"E91")}),-1.0]])]});
            var Q1;
            Q1=makeQuery(id+"F21.imprint","IMPRINT",FACE,{"disambiguationData":[TD([[makeQuery(id+"F21.imprint","IMPRINT",EDGE,{"derivedFrom":sQuery(id+"F21.wireOp",EDGE,"E94")}),-1.0]])]});
            extrude(context, id + "F23", {"entities" : qUnion([Q0, Q1]), "operationType" : NewBodyOperationType.REMOVE, "oppositeDirection" : true, "depth" : 25 * mm, "offsetDistance" : 25 * mm});
        }
        {
            var Q0;
            Q0=makeQuery(id+"F21.imprint","IMPRINT",FACE,{"disambiguationData":[TD([[makeQuery(id+"F21.imprint","IMPRINT",EDGE,{"derivedFrom":sQuery(id+"F21.wireOp",EDGE,"E92")}),-1.0]])]});
            var Q1;
            Q1=makeQuery(id+"F21.imprint","IMPRINT",FACE,{"disambiguationData":[TD([[makeQuery(id+"F21.imprint","IMPRINT",EDGE,{"derivedFrom":sQuery(id+"F21.wireOp",EDGE,"E95")}),-1.0]])]});
            extrude(context, id + "F24", {"entities" : qUnion([Q0, Q1]), "operationType" : NewBodyOperationType.REMOVE, "oppositeDirection" : true, "depth" : 2 * mm, "offsetDistance" : 25 * mm});
        }
        {
            var Q0;
            Q0=makeQuery(id+"F19.opExtrude","SWEPT_FACE",FACE,{"disambiguationData":[OSD([sQuery(id+"F0.wireOp",EDGE,"E55")])]});
            var sketch = newSketch(context, id + "F25", { "sketchPlane" : qUnion([Q0])});
            skPoint(sketch, "E97.0", {"position": v(163.12, 22) * mm});
            skPoint(sketch, "E97.1", {"position": v(163.12, 0) * mm});
            skLineSegment(sketch, "E98", {"start": v(163.12, 22) * mm, "end": v(163.12, 16) * mm, "construction": true});
            skLineSegment(sketch, "E99", {"start": v(163.12, 16) * mm, "end": v(171.12, 16) * mm, "construction": true});
            skLineSegment(sketch, "E100", {"start": v(163.12, 0) * mm, "end": v(163.12, 6) * mm, "construction": true});
            skLineSegment(sketch, "E101", {"start": v(163.12, 6) * mm, "end": v(171.12, 6) * mm, "construction": true});
            skCircle(sketch, "E102", {"center": v(171.12, 16) * mm, "radius": 1 * mm});
            skCircle(sketch, "E103", {"center": v(171.12, 16) * mm, "radius": 1.5 * mm});
            skCircle(sketch, "E104", {"center": v(171.12, 16) * mm, "radius": 3 * mm});
            skCircle(sketch, "E105", {"center": v(171.12, 6) * mm, "radius": 1 * mm});
            skCircle(sketch, "E106", {"center": v(171.12, 6) * mm, "radius": 1.5 * mm});
            skCircle(sketch, "E107", {"center": v(171.12, 6) * mm, "radius": 3 * mm});
            skSolve(sketch);
        }
        {
            var Q0;
            Q0=makeQuery(id+"F25.imprint","IMPRINT",FACE,{"disambiguationData":[TD([[makeQuery(id+"F25.imprint","IMPRINT",EDGE,{"derivedFrom":sQuery(id+"F25.wireOp",EDGE,"E102")}),1.0]])]});
            var Q1;
            Q1=makeQuery(id+"F25.imprint","IMPRINT",FACE,{"disambiguationData":[TD([[makeQuery(id+"F25.imprint","IMPRINT",EDGE,{"derivedFrom":sQuery(id+"F25.wireOp",EDGE,"E105")}),1.0]])]});
            extrude(context, id + "F26", {"entities" : qUnion([Q0, Q1]), "operationType" : NewBodyOperationType.REMOVE, "oppositeDirection" : true, "depth" : 10.3 * mm, "offsetDistance" : 25 * mm});
        }
        {
            var Q0;
            Q0=makeQuery(id+"F25.imprint","IMPRINT",FACE,{"disambiguationData":[TD([[makeQuery(id+"F25.imprint","IMPRINT",EDGE,{"derivedFrom":sQuery(id+"F25.wireOp",EDGE,"E102")}),-1.0]])]});
            var Q1;
            Q1=makeQuery(id+"F25.imprint","IMPRINT",FACE,{"disambiguationData":[TD([[makeQuery(id+"F25.imprint","IMPRINT",EDGE,{"derivedFrom":sQuery(id+"F25.wireOp",EDGE,"E105")}),-1.0]])]});
            extrude(context, id + "F27", {"entities" : qUnion([Q0, Q1]), "operationType" : NewBodyOperationType.REMOVE, "oppositeDirection" : true, "depth" : 8.2 * mm, "offsetDistance" : 25 * mm});
        }
        {
            var Q0;
            Q0=makeQuery(id+"F25.imprint","IMPRINT",FACE,{"disambiguationData":[TD([[makeQuery(id+"F25.imprint","IMPRINT",EDGE,{"derivedFrom":sQuery(id+"F25.wireOp",EDGE,"E103")}),-1.0]])]});
            var Q1;
            Q1=makeQuery(id+"F25.imprint","IMPRINT",FACE,{"disambiguationData":[TD([[makeQuery(id+"F25.imprint","IMPRINT",EDGE,{"derivedFrom":sQuery(id+"F25.wireOp",EDGE,"E106")}),-1.0]])]});
            extrude(context, id + "F28", {"entities" : qUnion([Q0, Q1]), "operationType" : NewBodyOperationType.REMOVE, "oppositeDirection" : true, "depth" : 2 * mm, "offsetDistance" : 25 * mm});
        }
    });
